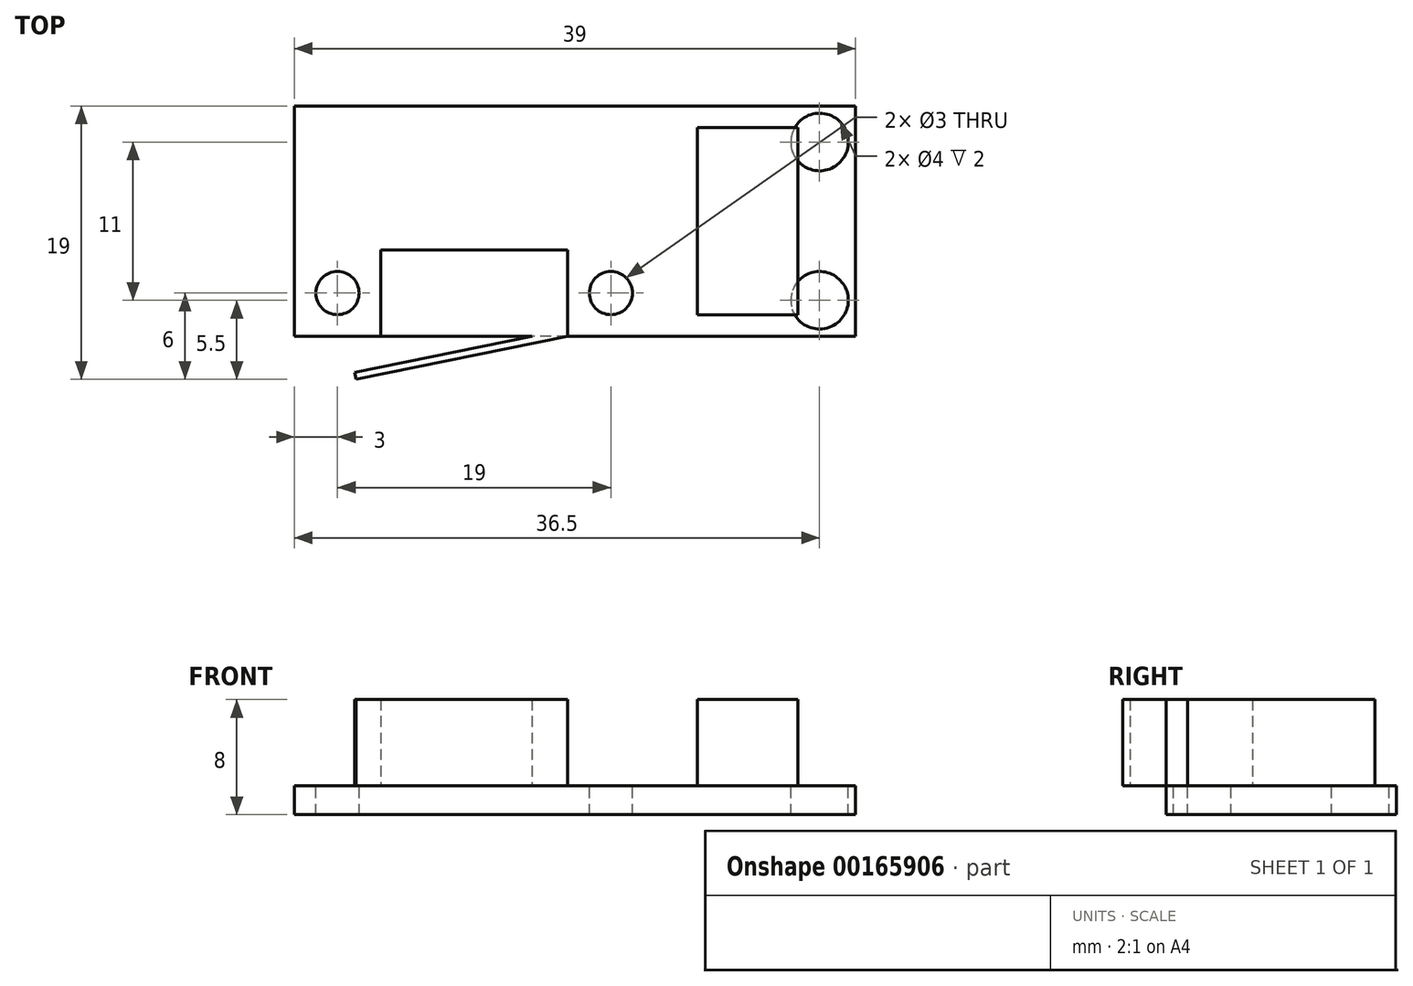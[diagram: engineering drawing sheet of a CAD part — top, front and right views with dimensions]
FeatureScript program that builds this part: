
annotation { "Feature Type Name" : "Feature", "Feature Type Description" : "" }
export const myFeature = defineFeature(function(context is Context, id is Id, definition is map)
    precondition{}
    {
        {
            var Q0;
            Q0=qCreatedBy(makeId("Top.planeOp"),FACE);
            var sketch = newSketch(context, id + "F0", { "sketchPlane" : qUnion([Q0])});
            skLineSegment(sketch, "E0.bottom", {"start": v(19.5, 8) * mm, "end": v(-19.5, 8) * mm});
            skLineSegment(sketch, "E0.top", {"start": v(19.5, -8) * mm, "end": v(-19.5, -8) * mm});
            skLineSegment(sketch, "E0.left", {"start": v(19.5, 8) * mm, "end": v(19.5, -8) * mm});
            skLineSegment(sketch, "E0.right", {"start": v(-19.5, 8) * mm, "end": v(-19.5, -8) * mm});
            skPoint(sketch, "E0.middle", {"position": v(0, 0) * mm});
            skSolve(sketch);
        }
        {
            var Q0;
            Q0=makeQuery(id+"F0.imprint","IMPRINT",FACE,{"disambiguationData":[TD([[makeQuery(id+"F0.imprint","IMPRINT",EDGE,{"derivedFrom":sQuery(id+"F0.wireOp",EDGE,"E0.bottom")}),1.0]])]});
            extrude(context, id + "F1", {"entities" : qUnion([Q0]), "depth" : 2 * mm});
        }
        {
            var Q0;
            Q0=makeQuery(id+"F1.opExtrude","CAP_FACE",FACE,{"disambiguationData":[OSD([sQuery(id+"F0.wireOp",EDGE,"E0.bottom"),sQuery(id+"F0.wireOp",EDGE,"E0.top"),sQuery(id+"F0.wireOp",EDGE,"E0.left"),sQuery(id+"F0.wireOp",EDGE,"E0.right")])],"isStart":false});
            var sketch = newSketch(context, id + "F2", { "sketchPlane" : qUnion([Q0])});
            skLineSegment(sketch, "E1.bottom", {"start": v(-13.5, -8) * mm, "end": v(-0.5, -8) * mm});
            skLineSegment(sketch, "E1.top", {"start": v(-13.5, -2) * mm, "end": v(-0.5, -2) * mm});
            skLineSegment(sketch, "E1.left", {"start": v(-13.5, -8) * mm, "end": v(-13.5, -2) * mm});
            skLineSegment(sketch, "E1.right", {"start": v(-0.5, -8) * mm, "end": v(-0.5, -2) * mm});
            skLineSegment(sketch, "E2", {"start": v(-19.5, 0) * mm, "end": v(19.5, 0) * mm, "construction": true});
            skLineSegment(sketch, "E3.bottom", {"start": v(8.5, 6.5) * mm, "end": v(15.5, 6.5) * mm});
            skLineSegment(sketch, "E3.top", {"start": v(8.5, -6.5) * mm, "end": v(15.5, -6.5) * mm});
            skLineSegment(sketch, "E3.left", {"start": v(8.5, 6.5) * mm, "end": v(8.5, -6.5) * mm});
            skLineSegment(sketch, "E3.right", {"start": v(15.5, 6.5) * mm, "end": v(15.5, -6.5) * mm});
            skPoint(sketch, "E3.middle", {"position": v(12, 0) * mm});
            skPoint(sketch, "E4", {"position": v(-16.5, -5) * mm});
            skPoint(sketch, "E5", {"position": v(17, -5.5) * mm});
            skLineSegment(sketch, "E6", {"start": v(-7, -8) * mm, "end": v(-7, 0) * mm, "construction": true});
            skPoint(sketch, "E7.MirrorP", {"position": v(2.5, -5) * mm});
            skPoint(sketch, "E8.MirrorP", {"position": v(17, 5.5) * mm});
            skLineSegment(sketch, "E9", {"start": v(-0.5, -8) * mm, "end": v(-15.2, -11) * mm});
            skLineSegment(sketch, "E10", {"start": v(-15.2, -11) * mm, "end": v(-15.3, -10.51) * mm});
            skLineSegment(sketch, "E11", {"start": v(-15.3, -10.51) * mm, "end": v(-3, -8) * mm});
            skSolve(sketch);
        }
        {
            var Q0;
            Q0=makeQuery(id+"F2.imprint","IMPRINT",FACE,{"disambiguationData":[TD([[makeQuery(id+"F2.imprint","IMPRINT",EDGE,{"derivedFrom":sQuery(id+"F2.wireOp",EDGE,"E1.bottom")}),-1.0]])]});
            var Q1;
            Q1=makeQuery(id+"F2.imprint","IMPRINT",FACE,{"disambiguationData":[TD([[makeQuery(id+"F2.imprint","IMPRINT",EDGE,{"derivedFrom":sQuery(id+"F2.wireOp",EDGE,"E3.bottom")}),-1.0]])]});
            var Q2;
            {var subQ0=sQuery(id+"F2.wireOp",EDGE,"E9");Q2=makeQuery(id+"F2.imprint","IMPRINT",FACE,{"disambiguationData":[TD([[makeQuery(id+"F2.imprint","IMPRINT",EDGE,{"derivedFrom":subQ0}),-1.0]])]});}
            extrude(context, id + "F3", {"entities" : qUnion([Q0, Q1, Q2]), "operationType" : NewBodyOperationType.ADD, "depth" : 6 * mm});
        }
        {
            var Q0;
            Q0=sQuery(id+"F2.wireOp",VERTEX,"E4");
            var Q1;
            Q1=sQuery(id+"F2.wireOp",VERTEX,"E7.MirrorP");
            var Q2;
            Q2=makeQuery(id+"F1.opExtrude","SWEPT_BODY",BODY,{"disambiguationData":[OSD([sQuery(id+"F0.wireOp",EDGE,"E0.bottom"),sQuery(id+"F0.wireOp",EDGE,"E0.top"),sQuery(id+"F0.wireOp",EDGE,"E0.left"),sQuery(id+"F0.wireOp",EDGE,"E0.right")])]});
            hole(context, id + "F4", {"style" : HoleStyle.SIMPLE, "endStyle" : HoleEndStyle.THROUGH, "standardTappedOrClearance" : lookupTablePath({ "standard" : "ISO", "size" : "3", "type" : "Drilled" }), "standardBlindInLast" : lookupTablePath({ "standard" : "ISO", "size" : "3", "type" : "Drilled" }), "holeDiameter" : 3 * mm, "locations" : qUnion([Q0, Q1]), "scope" : qUnion([Q2]), "isTappedThrough" : true});
        }
        {
            var Q0;
            Q0=sQuery(id+"F2.wireOp",VERTEX,"E8.MirrorP");
            var Q1;
            Q1=sQuery(id+"F2.wireOp",VERTEX,"E5");
            var Q2;
            Q2=makeQuery(id+"F1.opExtrude","SWEPT_BODY",BODY,{"disambiguationData":[OSD([sQuery(id+"F0.wireOp",EDGE,"E0.bottom"),sQuery(id+"F0.wireOp",EDGE,"E0.top"),sQuery(id+"F0.wireOp",EDGE,"E0.left"),sQuery(id+"F0.wireOp",EDGE,"E0.right")])]});
            hole(context, id + "F5", {"style" : HoleStyle.SIMPLE, "endStyle" : HoleEndStyle.THROUGH, "standardTappedOrClearance" : lookupTablePath({ "standard" : "ISO", "size" : "4", "type" : "Drilled" }), "standardBlindInLast" : lookupTablePath({ "standard" : "ISO", "size" : "4", "type" : "Drilled" }), "holeDiameter" : 4 * mm, "locations" : qUnion([Q0, Q1]), "scope" : qUnion([Q2]), "isTappedThrough" : true});
        }
    });
